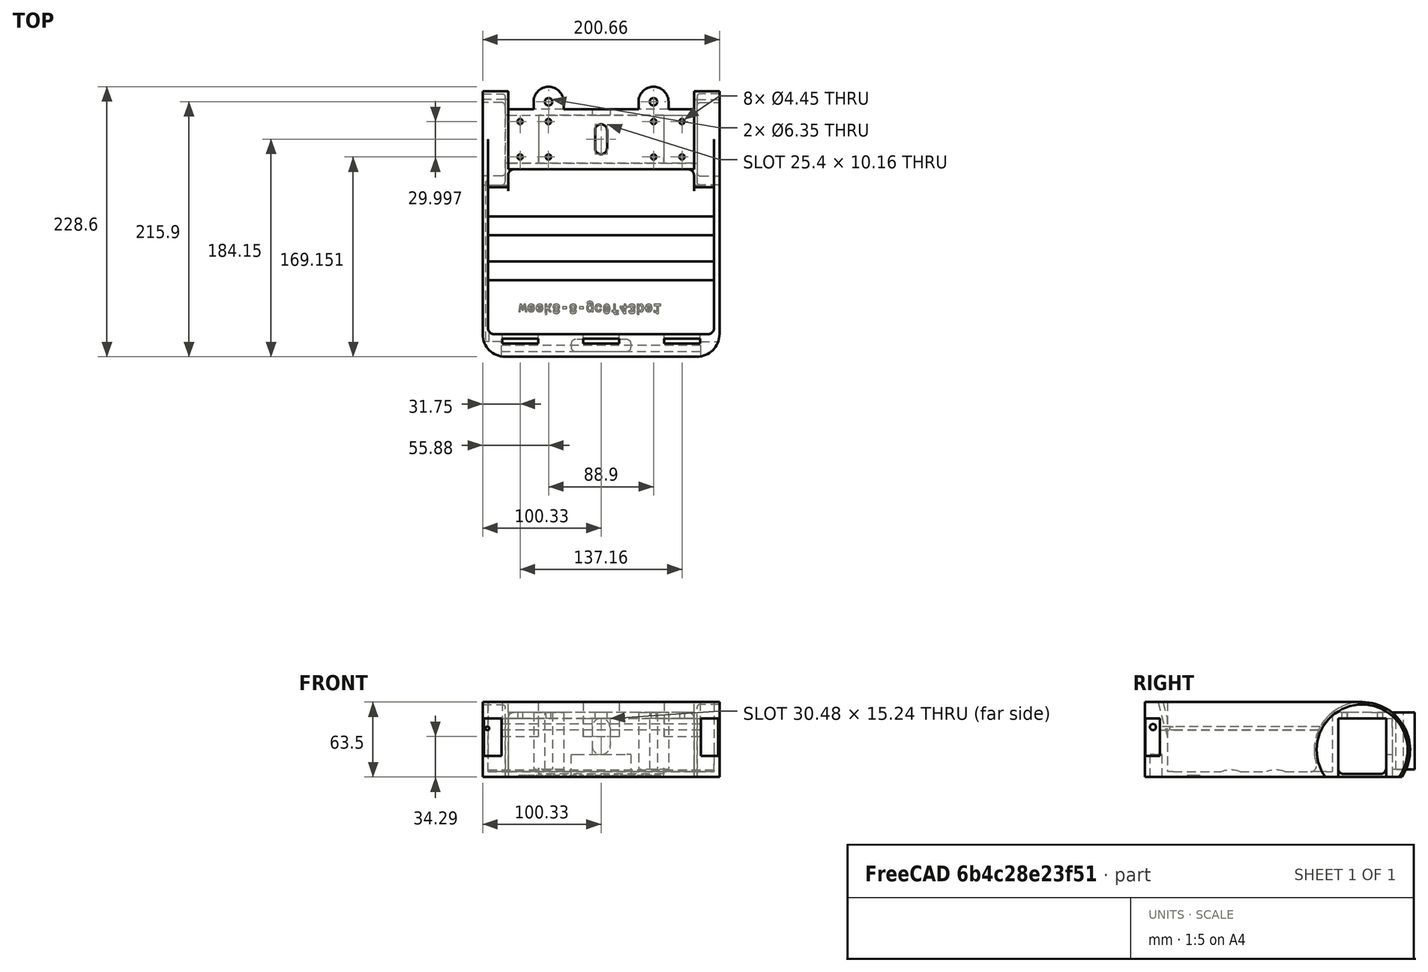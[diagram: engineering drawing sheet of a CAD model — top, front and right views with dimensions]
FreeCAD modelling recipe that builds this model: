
FCSTD DOCUMENT  (FreeCAD 0.20R27936 (Git))
Label: Frame
License: All rights reserved
LicenseURL: http://en.wikipedia.org/wiki/All_rights_reserved
objects: Sketcher::SketchObject×18, PartDesign::Pad×12, PartDesign::Pocket×7, PartDesign::Fillet×4, PartDesign::Plane×2, Part::Part2DObjectPython×1, PartDesign::Body×1
note: 68 computed .brp shape members not serialized (recipe doc carries the construction recipe); baked Part::Feature solids carry a one-line shape summary decoded from their .brp

FEATURE [Sketcher::SketchObject] Sketch
  FullyConstrained = true
  MapMode = 5
  Support = -> [XY_Plane]
  sketch-geometry (29):
    g0: LineSegment StartX=-78.74 StartY=-20.32 StartZ=0 EndX=-78.74 EndY=20.32 EndZ=0
    g1: LineSegment StartX=-78.74 StartY=20.32 StartZ=0 EndX=78.74 EndY=20.32 EndZ=0
    g2: LineSegment StartX=78.74 StartY=20.32 StartZ=0 EndX=78.74 EndY=-20.32 EndZ=0
    g3: LineSegment StartX=78.74 StartY=-20.32 StartZ=0 EndX=-78.74 EndY=-20.32 EndZ=0
    g4: GeomPoint X=0 Y=0 Z=0
    g5: LineSegment StartX=-68.58 StartY=14.9987 StartZ=0 EndX=-44.577 EndY=14.9987 EndZ=0
    g6: LineSegment StartX=-44.577 StartY=14.9987 StartZ=0 EndX=-44.577 EndY=-14.9987 EndZ=0
    g7: LineSegment StartX=-44.577 StartY=-14.9987 StartZ=0 EndX=-68.58 EndY=-14.9987 EndZ=0
    g8: LineSegment StartX=-68.58 StartY=-14.9987 StartZ=0 EndX=-68.58 EndY=14.9987 EndZ=0
    g9: LineSegment StartX=44.577 StartY=14.9987 StartZ=0 EndX=68.58 EndY=14.9987 EndZ=0
    g10: LineSegment StartX=68.58 StartY=14.9987 StartZ=0 EndX=68.58 EndY=-14.9987 EndZ=0
    g11: LineSegment StartX=68.58 StartY=-14.9987 StartZ=0 EndX=44.577 EndY=-14.9987 EndZ=0
    g12: LineSegment StartX=44.577 StartY=-14.9987 StartZ=0 EndX=44.577 EndY=14.9987 EndZ=0
    g13: Circle CenterX=-68.58 CenterY=14.9987 CenterZ=0 NormalX=0 NormalY=0 NormalZ=1 AngleXU=0 Radius=2.2225
    g14: Circle CenterX=-44.577 CenterY=14.9987 CenterZ=0 NormalX=0 NormalY=0 NormalZ=1 AngleXU=0 Radius=2.2225
    g15: Circle CenterX=-68.58 CenterY=-14.9987 CenterZ=0 NormalX=0 NormalY=0 NormalZ=1 AngleXU=0 Radius=2.2225
    g16: Circle CenterX=-44.577 CenterY=-14.9987 CenterZ=0 NormalX=0 NormalY=0 NormalZ=1 AngleXU=0 Radius=2.2225
    g17: Circle CenterX=44.577 CenterY=14.9987 CenterZ=0 NormalX=0 NormalY=0 NormalZ=1 AngleXU=0 Radius=2.2225
    g18: Circle CenterX=44.577 CenterY=-14.9987 CenterZ=0 NormalX=0 NormalY=0 NormalZ=1 AngleXU=0 Radius=2.2225
    g19: Circle CenterX=68.58 CenterY=14.9987 CenterZ=0 NormalX=0 NormalY=0 NormalZ=1 AngleXU=0 Radius=2.2225
    g20: Circle CenterX=68.58 CenterY=-14.9987 CenterZ=0 NormalX=0 NormalY=0 NormalZ=1 AngleXU=0 Radius=2.2225
    g21: LineSegment StartX=-68.58 StartY=0 StartZ=0 EndX=-78.74 EndY=0 EndZ=0
    g22: LineSegment StartX=68.58 StartY=0 StartZ=0 EndX=78.74 EndY=0 EndZ=0
    g23: ArcOfCircle CenterX=0 CenterY=7.62 CenterZ=0 NormalX=0 NormalY=0 NormalZ=1 AngleXU=0 Radius=5.08 StartAngle=0 EndAngle=3.14159
    g24: ArcOfCircle CenterX=0 CenterY=-7.62 CenterZ=0 NormalX=0 NormalY=0 NormalZ=1 AngleXU=0 Radius=5.08 StartAngle=3.14159 EndAngle=6.28319
    g25: LineSegment StartX=-5.08 StartY=7.62 StartZ=0 EndX=-5.08 EndY=-7.62 EndZ=0
    g26: LineSegment StartX=5.08 StartY=7.62 StartZ=0 EndX=5.08 EndY=-7.62 EndZ=0
    g27: LineSegment StartX=0 StartY=7.62 StartZ=0 EndX=0 EndY=0 EndZ=0
    g28: LineSegment StartX=0 StartY=0 StartZ=0 EndX=0 EndY=-7.62 EndZ=0
  constraints (70):
    c: Coincident(g0,g1)
    c: Coincident(g1,g2)
    c: Coincident(g2,g3)
    c: Coincident(g3,g0)
    c: Horizontal(g1)
    c: Horizontal(g3)
    c: Vertical(g0)
    c: Vertical(g2)
    c: Symmetric(g1,g0,g4)
    c: Coincident(g4,g-1)
    c: Distance(g1) = 157.48
    c: Distance(g0) = 40.64
    c: Coincident(g5,g6)
    c: Coincident(g6,g7)
    c: Coincident(g7,g8)
    c: Coincident(g8,g5)
    c: Horizontal(g5)
    c: Horizontal(g7)
    c: Vertical(g8)
    c: Coincident(g9,g10)
    c: Coincident(g10,g11)
    c: Coincident(g11,g12)
    c: Coincident(g12,g9)
    c: Horizontal(g9)
    c: Horizontal(g11)
    c: Vertical(g10)
    c: Distance(g6) = 29.9974
    c: Symmetric(g5,g6,g-1)
    c: Equal(g12,g6)
    c: Symmetric(g9,g11,g-1)
    c: Equal(g9,g5)
    c: Distance(g5) = 24.003
    c: Coincident(g13,g5)
    c: Coincident(g14,g5)
    c: Coincident(g15,g7)
    c: Coincident(g16,g6)
    c: Coincident(g17,g9)
    c: Coincident(g18,g11)
    c: Coincident(g19,g9)
    c: Coincident(g20,g10)
    c: Equal(g20,g18)
    c: Equal(g18,g17)
    c: Equal(g17,g19)
    c: Equal(g19,g14)
    c: Equal(g14,g13)
    c: Equal(g13,g15)
    c: Equal(g15,g16)
    c: Diameter(g16) = 4.445
    c: PointOnObject(g21,g8)
    c: PointOnObject(g21,g0)
    c: PointOnObject(g22,g10)
    c: PointOnObject(g22,g2)
    c: Tangent(g-1,g22)
    c: Tangent(g-1,g21)
    c: Equal(g21,g22)
    c: Distance(g21) = 10.16
    c: PointOnObject(g23,g-2)
    c: PointOnObject(g24,g-2)
    c: Vertical(g25)
    c: Tangent(g26,g24) = 1.5708
    c: Tangent(g26,g23) = 1.5708
    c: Tangent(g25,g23) = -1.5708
    c: Tangent(g25,g24) = -1.5708
    c: Radius(g23) = 5.08
    c: Coincident(g27,g23)
    c: Coincident(g27,g4)
    c: Coincident(g28,g4)
    c: Coincident(g28,g24)
    c: Equal(g28,g27)
    c: Distance(g27) = 7.62
FEATURE [PartDesign::Pad] Pad
  Direction = (0,0,1)
  Length = 5.08
  Length2 = 10.0076
  Profile = -> Sketch
  ReferenceAxis = -> Sketch [N_Axis]
  Type = 0
FEATURE [Sketcher::SketchObject] Sketch001
  ExternalGeometry = -> [Pad]
  FullyConstrained = true
  MapMode = 5
  Placement = pos=(0,0,5.08) rot=(0,0,1;0rad)
  Support = -> [Pad]
  sketch-geometry (8):
    g0: LineSegment StartX=-78.74 StartY=20.32 StartZ=0 EndX=78.74 EndY=20.32 EndZ=0
    g1: LineSegment StartX=78.74 StartY=20.32 StartZ=0 EndX=78.74 EndY=25.4 EndZ=0
    g2: LineSegment StartX=78.74 StartY=25.4 StartZ=0 EndX=-78.74 EndY=25.4 EndZ=0
    g3: LineSegment StartX=-78.74 StartY=25.4 StartZ=0 EndX=-78.74 EndY=20.32 EndZ=0
    g4: LineSegment StartX=-78.74 StartY=-20.32 StartZ=0 EndX=78.74 EndY=-20.32 EndZ=0
    g5: LineSegment StartX=78.74 StartY=-20.32 StartZ=0 EndX=78.74 EndY=-25.4 EndZ=0
    g6: LineSegment StartX=78.74 StartY=-25.4 StartZ=0 EndX=-78.74 EndY=-25.4 EndZ=0
    g7: LineSegment StartX=-78.74 StartY=-25.4 StartZ=0 EndX=-78.74 EndY=-20.32 EndZ=0
  constraints (20):
    c: Coincident(g0,g1)
    c: Coincident(g1,g2)
    c: Coincident(g2,g3)
    c: Coincident(g3,g0)
    c: Horizontal(g0)
    c: Horizontal(g2)
    c: Vertical(g3)
    c: Coincident(g0,g-4)
    c: Coincident(g4,g5)
    c: Coincident(g5,g6)
    c: Coincident(g6,g7)
    c: Coincident(g7,g4)
    c: Horizontal(g4)
    c: Horizontal(g6)
    c: Vertical(g7)
    c: Coincident(g4,g-5)
    c: Tangent(g5,g-3)
    c: Tangent(g-3,g1)
    c: Equal(g1,g5)
    c: Distance(g3) = 5.08
FEATURE [PartDesign::Pad] Pad001
  BaseFeature = -> Pad
  Direction = (0,0,1)
  Length = 54.61
  Length2 = 10.0076
  Profile = -> Sketch001
  ReferenceAxis = -> Sketch001 [N_Axis]
  Reversed = true
  Type = 0
FEATURE [Sketcher::SketchObject] Sketch002
  ExternalGeometry = -> [Pad001]
  FullyConstrained = true
  MapMode = 5
  Placement = pos=(0,20.32,0) rot=(1,0,0;1.5708rad)
  Support = -> [Pad001]
  sketch-geometry (4):
    g0: LineSegment StartX=-53.0225 StartY=-49.53 StartZ=0 EndX=53.0225 EndY=-49.53 EndZ=0
    g1: LineSegment StartX=53.0225 StartY=-49.53 StartZ=0 EndX=53.0225 EndY=-46.99 EndZ=0
    g2: LineSegment StartX=53.0225 StartY=-46.99 StartZ=0 EndX=-53.0225 EndY=-46.99 EndZ=0
    g3: LineSegment StartX=-53.0225 StartY=-46.99 StartZ=0 EndX=-53.0225 EndY=-49.53 EndZ=0
  constraints (11):
    c: Coincident(g0,g1)
    c: Coincident(g1,g2)
    c: Coincident(g2,g3)
    c: Coincident(g3,g0)
    c: Horizontal(g2)
    c: Vertical(g1)
    c: Vertical(g3)
    c: Distance(g0) = 106.045
    c: Tangent(g0,g-3)
    c: Symmetric(g0,g0,g-2)
    c: Distance(g3) = 2.54
FEATURE [PartDesign::Pad] Pad002
  BaseFeature = -> Pad001
  Direction = (0,-1,2e-16)
  Length = 10.0076
  Length2 = 10.0076
  Profile = -> Sketch002
  ReferenceAxis = -> Sketch002 [N_Axis]
  Type = 3
  UpToFace = -> Pad001 [Face7]
FEATURE [PartDesign::Fillet] Fillet
  Base = -> Pad002 [Edge49,Edge61]
  BaseFeature = -> Pad002
  Radius = 5.08
  SupportTransform = false
  UseAllEdges = false
FEATURE [Sketcher::SketchObject] Sketch003
  ExternalGeometry = -> [Fillet]
  FullyConstrained = true
  MapMode = 5
  Placement = pos=(-78.74,0,0) rot=(0.57735,-0.57735,-0.57735;2.0944rad)
  Support = -> [Fillet]
  sketch-geometry (7):
    g0: Circle CenterX=0 CenterY=-26.67 CenterZ=0 NormalX=0 NormalY=0 NormalZ=1 AngleXU=0 Radius=40.64
    g1: ArcOfCircle CenterX=0 CenterY=-26.67 CenterZ=0 NormalX=0 NormalY=0 NormalZ=1 AngleXU=0 Radius=40.64 StartAngle=5.68578 EndAngle=10.0222
    g2: LineSegment StartX=-33.601 StartY=-49.53 StartZ=0 EndX=-20.32 EndY=-49.53 EndZ=0
    g3: LineSegment StartX=-20.32 StartY=-49.53 StartZ=0 EndX=-20.32 EndY=0 EndZ=0
    g4: LineSegment StartX=-20.32 StartY=0 StartZ=0 EndX=20.32 EndY=0 EndZ=0
    g5: LineSegment StartX=20.32 StartY=0 StartZ=0 EndX=20.32 EndY=-49.53 EndZ=0
    g6: LineSegment StartX=20.32 StartY=-49.53 StartZ=0 EndX=33.601 EndY=-49.53 EndZ=0
  constraints (19):
    c: PointOnObject(g0,g-2)
    c: Distance(g0,g-3) = 31.75
    c: Diameter(g0) = 81.28
    c: Coincident(g1,g0)
    c: PointOnObject(g1,g0)
    c: Coincident(g2,g1)
    c: Coincident(g6,g1)
    c: Coincident(g3,g-4)
    c: PointOnObject(g3,g-1)
    c: Vertical(g3)
    c: Coincident(g4,g3)
    c: PointOnObject(g4,g-1)
    c: Coincident(g5,g4)
    c: Coincident(g5,g-4)
    c: Vertical(g5)
    c: Tangent(g6,g-4) = -1.5708
    c: Coincident(g6,g5)
    c: Coincident(g2,g3)
    c: Tangent(g2,g-4)
FEATURE [PartDesign::Pad] Pad003
  BaseFeature = -> Fillet
  Direction = (-1,0,0)
  Length = 2.54
  Length2 = 10.0076
  Profile = -> Sketch003
  ReferenceAxis = -> Sketch003 [N_Axis]
  Type = 0
FEATURE [Sketcher::SketchObject] Sketch004
  ExternalGeometry = -> [Pad003]
  FullyConstrained = true
  MapMode = 5
  Placement = pos=(78.74,0,0) rot=(0.57735,0.57735,0.57735;2.0944rad)
  Support = -> [Pad003]
  sketch-geometry (6):
    g0: LineSegment StartX=-20.32 StartY=-49.53 StartZ=0 EndX=-33.601 EndY=-49.53 EndZ=0
    g1: LineSegment StartX=20.32 StartY=-49.53 StartZ=0 EndX=33.601 EndY=-49.53 EndZ=0
    g2: LineSegment StartX=20.32 StartY=-49.53 StartZ=0 EndX=20.32 EndY=0 EndZ=0
    g3: LineSegment StartX=20.32 StartY=0 StartZ=0 EndX=-20.32 EndY=0 EndZ=0
    g4: LineSegment StartX=-20.32 StartY=0 StartZ=0 EndX=-20.32 EndY=-49.53 EndZ=0
    g5: ArcOfCircle CenterX=0 CenterY=-26.67 CenterZ=0 NormalX=0 NormalY=0 NormalZ=1 AngleXU=0 Radius=40.64 StartAngle=5.68578 EndAngle=10.0222
  constraints (16):
    c: Coincident(g0,g-3)
    c: Coincident(g0,g-5)
    c: Coincident(g1,g-4)
    c: Horizontal(g1)
    c: Coincident(g2,g1)
    c: PointOnObject(g2,g-1)
    c: Vertical(g2)
    c: Coincident(g3,g2)
    c: PointOnObject(g3,g-1)
    c: Coincident(g4,g3)
    c: Coincident(g4,g0)
    c: Vertical(g4)
    c: PointOnObject(g5,g-2)
    c: Coincident(g5,g0)
    c: Coincident(g5,g1)
    c: Equal(g5,g-5)
FEATURE [PartDesign::Pad] Pad004
  BaseFeature = -> Pad003
  Direction = (1,0,0)
  Length = 2.54
  Length2 = 10.0076
  Profile = -> Sketch004
  ReferenceAxis = -> Sketch004 [N_Axis]
  Type = 0
FEATURE [Sketcher::SketchObject] Sketch005
  ExternalGeometry = -> [Pad004]
  FullyConstrained = true
  MapMode = 5
  Placement = pos=(-81.28,0,0) rot=(0.57735,-0.57735,-0.57735;2.0944rad)
  Support = -> [Pad004]
  sketch-geometry (4):
    g0: ArcOfCircle CenterX=4.7e-15 CenterY=-26.67 CenterZ=0 NormalX=0 NormalY=0 NormalZ=1 AngleXU=0 Radius=40.64 StartAngle=5.68578 EndAngle=10.0222
    g1: ArcOfCircle CenterX=4.7e-15 CenterY=-26.67 CenterZ=0 NormalX=0 NormalY=0 NormalZ=1 AngleXU=0 Radius=38.5664 StartAngle=5.64872 EndAngle=10.0592
    g2: LineSegment StartX=-33.601 StartY=-49.53 StartZ=0 EndX=-31.061 EndY=-49.53 EndZ=0
    g3: LineSegment StartX=31.061 StartY=-49.53 StartZ=0 EndX=33.601 EndY=-49.53 EndZ=0
  constraints (11):
    c: Coincident(g1,g0)
    c: Coincident(g2,g0)
    c: Coincident(g2,g1)
    c: Coincident(g3,g1)
    c: Coincident(g3,g0)
    c: Horizontal(g3)
    c: Horizontal(g2)
    c: Distance(g2) = 2.54
    c: Coincident(g0,g-3)
    c: Coincident(g0,g-3)
    c: Equal(g0,g-3)
FEATURE [PartDesign::Pad] Pad005
  BaseFeature = -> Pad004
  Direction = (-1,0,0)
  Length = 19.05
  Length2 = 10.0076
  Profile = -> Sketch005
  ReferenceAxis = -> Sketch005 [N_Axis]
  Type = 0
FEATURE [Sketcher::SketchObject] Sketch006
  ExternalGeometry = -> [Pad005]
  FullyConstrained = true
  MapMode = 5
  Placement = pos=(81.28,0,0) rot=(0.57735,0.57735,0.57735;2.0944rad)
  Support = -> [Pad005]
  sketch-geometry (4):
    g0: ArcOfCircle CenterX=-3.6e-15 CenterY=-26.67 CenterZ=0 NormalX=0 NormalY=0 NormalZ=1 AngleXU=0 Radius=40.64 StartAngle=5.68578 EndAngle=10.0222
    g1: ArcOfCircle CenterX=-3.6e-15 CenterY=-26.67 CenterZ=0 NormalX=0 NormalY=0 NormalZ=1 AngleXU=0 Radius=38.5664 StartAngle=5.64872 EndAngle=10.0592
    g2: LineSegment StartX=31.061 StartY=-49.53 StartZ=0 EndX=33.601 EndY=-49.53 EndZ=0
    g3: LineSegment StartX=-33.601 StartY=-49.53 StartZ=0 EndX=-31.061 EndY=-49.53 EndZ=0
  constraints (10):
    c: Coincident(g0,g-4)
    c: Coincident(g0,g-4)
    c: Coincident(g0,g-4)
    c: Coincident(g1,g0)
    c: Coincident(g1,g-3)
    c: Coincident(g1,g-3)
    c: Coincident(g2,g1)
    c: Coincident(g2,g0)
    c: Coincident(g3,g0)
    c: Coincident(g3,g1)
FEATURE [PartDesign::Pad] Pad006
  BaseFeature = -> Pad005
  Direction = (1,0,0)
  Length = 19.05
  Length2 = 10.0076
  Profile = -> Sketch006
  ReferenceAxis = -> Sketch006 [N_Axis]
  Type = 0
FEATURE [PartDesign::Fillet] Fillet001
  Base = -> Pad006 [Edge101,Edge71]
  BaseFeature = -> Pad006
  Radius = 2.54
  SupportTransform = false
  UseAllEdges = false
FEATURE [PartDesign::Plane] DatumPlane
  AttachmentOffset = pos=(0,0,165.1) rot=(0,0,1;0rad)
  Length = 60
  MapMode = 5
  Placement = pos=(0,-165.1,-3.67e-14) rot=(1,0,0;1.5708rad)
  ResizeMode = 0
  Support = -> [XZ_Plane]
  Width = 60
FEATURE [Sketcher::SketchObject] Sketch007
  ExternalGeometry = -> [Fillet001]
  FullyConstrained = true
  MapMode = 5
  Placement = pos=(0,-165.1,-3.67e-14) rot=(1,0,0;1.5708rad)
  Support = -> [DatumPlane]
  sketch-geometry (9):
    g0: LineSegment StartX=-100.33 StartY=13.97 StartZ=0 EndX=-100.33 EndY=-49.53 EndZ=0
    g1: LineSegment StartX=-100.33 StartY=-49.53 StartZ=0 EndX=100.33 EndY=-49.53 EndZ=0
    g2: LineSegment StartX=100.33 StartY=-49.53 StartZ=0 EndX=100.33 EndY=13.97 EndZ=0
    g3: LineSegment StartX=100.33 StartY=13.97 StartZ=0 EndX=95.758 EndY=13.97 EndZ=0
    g4: LineSegment StartX=95.758 StartY=13.97 StartZ=0 EndX=95.758 EndY=-44.958 EndZ=0
    g5: LineSegment StartX=95.758 StartY=-44.958 StartZ=0 EndX=-95.758 EndY=-44.958 EndZ=0
    g6: LineSegment StartX=-95.758 StartY=-44.958 StartZ=0 EndX=-95.758 EndY=13.97 EndZ=0
    g7: LineSegment StartX=-95.758 StartY=13.97 StartZ=0 EndX=-100.33 EndY=13.97 EndZ=0
    g8: LineSegment StartX=0 StartY=-49.53 StartZ=0 EndX=0 EndY=-44.958 EndZ=0
  constraints (23):
    c: Coincident(g0,g-3)
    c: Coincident(g0,g-3)
    c: Coincident(g1,g0)
    c: Coincident(g1,g-4)
    c: Coincident(g2,g1)
    c: Vertical(g2)
    c: Coincident(g3,g2)
    c: Horizontal(g3)
    c: Coincident(g4,g3)
    c: Vertical(g4)
    c: Coincident(g5,g4)
    c: Horizontal(g5)
    c: Coincident(g6,g5)
    c: Vertical(g6)
    c: Coincident(g7,g6)
    c: Coincident(g7,g0)
    c: PointOnObject(g8,g1)
    c: PointOnObject(g8,g5)
    c: Tangent(g8,g-2) = -1.5708
    c: Equal(g8,g7)
    c: Equal(g7,g3)
    c: Distance(g7) = 4.572
    c: Tangent(g3,g7)
FEATURE [PartDesign::Pad] Pad007
  BaseFeature = -> Fillet001
  Direction = (0,-1,-2e-16)
  Length = 10.0076
  Length2 = 10.0076
  Profile = -> Sketch007
  ReferenceAxis = -> Sketch007 [N_Axis]
  Reversed = true
  Type = 3
  UpToFace = -> Fillet001 [Face61]
FEATURE [Sketcher::SketchObject] Sketch008
  ExternalGeometry = -> [Pad007]
  FullyConstrained = true
  MapMode = 5
  Placement = pos=(0,-25.4,0) rot=(1,0,0;1.5708rad)
  Support = -> [Pad007]
  sketch-geometry (4):
    g0: LineSegment StartX=78.74 StartY=-44.958 StartZ=0 EndX=-78.74 EndY=-44.958 EndZ=0
    g1: LineSegment StartX=-78.74 StartY=-44.958 StartZ=0 EndX=-78.74 EndY=-49.53 EndZ=0
    g2: LineSegment StartX=-78.74 StartY=-49.53 StartZ=0 EndX=78.74 EndY=-49.53 EndZ=0
    g3: LineSegment StartX=78.74 StartY=-49.53 StartZ=0 EndX=78.74 EndY=-44.958 EndZ=0
  constraints (10):
    c: Coincident(g0,g1)
    c: Coincident(g1,g2)
    c: Coincident(g2,g3)
    c: Coincident(g3,g0)
    c: Horizontal(g0)
    c: Horizontal(g2)
    c: Vertical(g1)
    c: Vertical(g3)
    c: Coincident(g0,g-4)
    c: Coincident(g1,g-3)
FEATURE [PartDesign::Pad] Pad008
  BaseFeature = -> Pad007
  Direction = (0,-1,2e-16)
  Length = 12.7
  Length2 = 10.0076
  Profile = -> Sketch008
  ReferenceAxis = -> Sketch008 [N_Axis]
  Type = 0
FEATURE [Sketcher::SketchObject] Sketch009
  ExternalGeometry = -> [Pad008]
  FullyConstrained = false
  MapMode = 5
  Placement = pos=(95.758,0,0) rot=(0.57735,-0.57735,-0.57735;2.0944rad)
  Support = -> [Pad008]
  sketch-geometry (5):
    g0: ArcOfCircle CenterX=73.2715 CenterY=-66.3764 CenterZ=0 NormalX=0 NormalY=0 NormalZ=1 AngleXU=0 Radius=22.86 StartAngle=1.21376 EndAngle=1.92783
    g1: ArcOfCircle CenterX=111.371 CenterY=-66.3764 CenterZ=0 NormalX=0 NormalY=0 NormalZ=1 AngleXU=0 Radius=22.86 StartAngle=1.21376 EndAngle=1.92783
    g2: LineSegment StartX=73.2715 StartY=-66.3764 StartZ=0 EndX=111.371 EndY=-66.3764 EndZ=0
    g3: LineSegment StartX=65.2819 StartY=-44.958 StartZ=0 EndX=81.2611 EndY=-44.958 EndZ=0
    g4: LineSegment StartX=103.382 StartY=-44.958 StartZ=0 EndX=119.361 EndY=-44.958 EndZ=0
  constraints (14):
    c: PointOnObject(g0,g-3)
    c: PointOnObject(g0,g-3)
    c: PointOnObject(g1,g-3)
    c: PointOnObject(g1,g-3)
    c: Equal(g1,g0)
    c: Coincident(g2,g0)
    c: Coincident(g2,g1)
    c: Horizontal(g2)
    c: Distance(g2) = 38.1
    c: Radius(g0) = 22.86
    c: Coincident(g3,g0)
    c: Coincident(g3,g0)
    c: Coincident(g4,g1)
    c: Coincident(g4,g1)
FEATURE [PartDesign::Pad] Pad009
  BaseFeature = -> Pad008
  Direction = (-1,0,0)
  Length = 10.0076
  Length2 = 10.0076
  Profile = -> Sketch009
  ReferenceAxis = -> Sketch009 [N_Axis]
  Type = 3
  UpToFace = -> Pad008 [Face37]
FEATURE [Sketcher::SketchObject] Sketch010
  ExternalGeometry = -> [Pad009]
  FullyConstrained = true
  MapMode = 5
  Placement = pos=(1.05e-14,1.1e-14,-49.53) rot=(1,0,0;3.14159rad)
  Support = -> [Pad009]
  sketch-geometry (4):
    g0: ArcOfCircle CenterX=-81.28 CenterY=165.1 CenterZ=0 NormalX=0 NormalY=0 NormalZ=1 AngleXU=0 Radius=19.05 StartAngle=1.5708 EndAngle=3.14159
    g1: ArcOfCircle CenterX=81.28 CenterY=165.1 CenterZ=0 NormalX=0 NormalY=0 NormalZ=1 AngleXU=0 Radius=19.05 StartAngle=-9e-16 EndAngle=1.5708
    g2: LineSegment StartX=100.33 StartY=165.1 StartZ=0 EndX=-100.33 EndY=165.1 EndZ=0
    g3: LineSegment StartX=-81.28 StartY=184.15 StartZ=0 EndX=81.28 EndY=184.15 EndZ=0
  constraints (10):
    c: Coincident(g2,g1)
    c: Coincident(g2,g0)
    c: Horizontal(g3)
    c: Tangent(g3,g1) = 1.5708
    c: Tangent(g3,g0) = 1.5708
    c: Coincident(g0,g-4)
    c: Coincident(g1,g-3)
    c: Radius(g1) = 19.05
    c: PointOnObject(g1,g2)
    c: Equal(g0,g1)
FEATURE [PartDesign::Pad] Pad010
  BaseFeature = -> Pad009
  Direction = (2e-16,2e-16,-1)
  Length = 10.0076
  Length2 = 10.0076
  Profile = -> Sketch010
  ReferenceAxis = -> Sketch010 [N_Axis]
  Type = 3
  UpToFace = -> Pad009 [Face38]
FEATURE [PartDesign::Plane] DatumPlane001
  AttachmentOffset = pos=(0,0,50.8) rot=(1,0,0;0.261799rad)
  Length = 61.0668
  MapMode = 5
  Placement = pos=(1.258e-13,-1.44e-14,64.77) rot=(1,0,0;0.261799rad)
  ResizeMode = 0
  Support = -> [Pad010]
  Width = 72.3041
FEATURE [Sketcher::SketchObject] Sketch011
  ExternalGeometry = -> [Pad010]
  FullyConstrained = true
  MapMode = 5
  Placement = pos=(1.258e-13,-1.78e-14,64.77) rot=(1,0,0;0.261799rad)
  Support = -> [DatumPlane001]
  sketch-geometry (14):
    g0: LineSegment StartX=-83.82 StartY=-176.178 StartZ=0 EndX=-53.34 EndY=-176.178 EndZ=0
    g1: LineSegment StartX=-53.34 StartY=-176.178 StartZ=0 EndX=-53.34 EndY=-180.242 EndZ=0
    g2: LineSegment StartX=-53.34 StartY=-180.242 StartZ=0 EndX=-83.82 EndY=-180.242 EndZ=0
    g3: LineSegment StartX=-83.82 StartY=-180.242 StartZ=0 EndX=-83.82 EndY=-176.178 EndZ=0
    g4: LineSegment StartX=-15.24 StartY=-176.178 StartZ=0 EndX=15.24 EndY=-176.178 EndZ=0
    g5: LineSegment StartX=15.24 StartY=-176.178 StartZ=0 EndX=15.24 EndY=-180.242 EndZ=0
    g6: LineSegment StartX=15.24 StartY=-180.242 StartZ=0 EndX=-15.24 EndY=-180.242 EndZ=0
    g7: LineSegment StartX=-15.24 StartY=-180.242 StartZ=0 EndX=-15.24 EndY=-176.178 EndZ=0
    g8: LineSegment StartX=53.34 StartY=-176.178 StartZ=0 EndX=83.82 EndY=-176.178 EndZ=0
    g9: LineSegment StartX=83.82 StartY=-176.178 StartZ=0 EndX=83.82 EndY=-180.242 EndZ=0
    g10: LineSegment StartX=83.82 StartY=-180.242 StartZ=0 EndX=53.34 EndY=-180.242 EndZ=0
    g11: LineSegment StartX=53.34 StartY=-180.242 StartZ=0 EndX=53.34 EndY=-176.178 EndZ=0
    g12: LineSegment StartX=53.34 StartY=-176.178 StartZ=0 EndX=15.24 EndY=-176.178 EndZ=0
    g13: LineSegment StartX=-15.24 StartY=-176.178 StartZ=0 EndX=-53.34 EndY=-176.178 EndZ=0
  constraints (37):
    c: Coincident(g0,g1)
    c: Coincident(g1,g2)
    c: Coincident(g2,g3)
    c: Coincident(g3,g0)
    c: Horizontal(g2)
    c: Vertical(g1)
    c: Vertical(g3)
    c: Coincident(g4,g5)
    c: Coincident(g5,g6)
    c: Coincident(g6,g7)
    c: Coincident(g7,g4)
    c: Horizontal(g6)
    c: Vertical(g5)
    c: Vertical(g7)
    c: Coincident(g8,g9)
    c: Coincident(g9,g10)
    c: Coincident(g10,g11)
    c: Coincident(g11,g8)
    c: Horizontal(g10)
    c: Vertical(g9)
    c: Vertical(g11)
    c: Equal(g11,g5)
    c: Equal(g5,g1)
    c: Tangent(g0,g4)
    c: Tangent(g4,g8)
    c: Distance(g9) = 4.064
    c: Equal(g8,g4)
    c: Equal(g4,g0)
    c: Symmetric(g4,g4,g-2)
    c: Coincident(g12,g8)
    c: Coincident(g12,g4)
    c: Coincident(g13,g4)
    c: Coincident(g13,g0)
    c: Equal(g13,g12)
    c: Distance(g4,g-3) = 3.556
    c: Distance(g13) = 38.1
    c: Distance(g6) = 30.48
FEATURE [PartDesign::Pocket] Pocket
  BaseFeature = -> Pad010
  Direction = (-1.9e-15,0.258819,-0.965926)
  Length = 55.8038
  Length2 = 5.0038
  Profile = -> Sketch011
  ReferenceAxis = -> Sketch011 [N_Axis]
  Type = 0
FEATURE [Sketcher::SketchObject] Sketch012
  FullyConstrained = true
  MapMode = 5
  Placement = pos=(0,-184.15,-4.09e-14) rot=(1,0,0;1.5708rad)
  Support = -> [Pocket]
  sketch-geometry (8):
    g0: LineSegment StartX=84.455 StartY=0 StartZ=0 EndX=100.965 EndY=0 EndZ=0
    g1: LineSegment StartX=100.965 StartY=0 StartZ=0 EndX=100.965 EndY=-31.75 EndZ=0
    g2: LineSegment StartX=100.965 StartY=-31.75 StartZ=0 EndX=84.455 EndY=-31.75 EndZ=0
    g3: LineSegment StartX=84.455 StartY=-31.75 StartZ=0 EndX=84.455 EndY=0 EndZ=0
    g4: LineSegment StartX=-84.455 StartY=0 StartZ=0 EndX=-100.965 EndY=0 EndZ=0
    g5: LineSegment StartX=-100.965 StartY=0 StartZ=0 EndX=-100.965 EndY=-31.75 EndZ=0
    g6: LineSegment StartX=-100.965 StartY=-31.75 StartZ=0 EndX=-84.455 EndY=-31.75 EndZ=0
    g7: LineSegment StartX=-84.455 StartY=-31.75 StartZ=0 EndX=-84.455 EndY=0 EndZ=0
  constraints (22):
    c: Coincident(g0,g1)
    c: Coincident(g1,g2)
    c: Coincident(g2,g3)
    c: Coincident(g3,g0)
    c: Horizontal(g2)
    c: Vertical(g1)
    c: Vertical(g3)
    c: Coincident(g4,g5)
    c: Coincident(g5,g6)
    c: Coincident(g6,g7)
    c: Coincident(g7,g4)
    c: Horizontal(g6)
    c: Vertical(g5)
    c: Vertical(g7)
    c: Equal(g7,g3)
    c: Tangent(g0,g4)
    c: PointOnObject(g0,g-1)
    c: Distance(g3) = 31.75
    c: Distance(g2) = 16.51
    c: Symmetric(g4,g0,g-2)
    c: Distance(g4,g0) = 168.91
    c: Equal(g4,g0)
FEATURE [PartDesign::Pocket] Pocket001
  BaseFeature = -> Pocket
  Direction = (0,1,2e-16)
  Length = 12.7
  Length2 = 5.0038
  Profile = -> Sketch012
  ReferenceAxis = -> Sketch012 [N_Axis]
  Type = 0
FEATURE [Sketcher::SketchObject] Sketch013
  ExternalGeometry = -> [Pocket001]
  FullyConstrained = true
  MapMode = 5
  Placement = pos=(0,0,5.08) rot=(0,0,1;0rad)
  Support = -> [Pocket001]
  sketch-geometry (10):
    g0: ArcOfCircle CenterX=-44.45 CenterY=31.75 CenterZ=0 NormalX=0 NormalY=0 NormalZ=1 AngleXU=0 Radius=12.7 StartAngle=2e-16 EndAngle=3.14159
    g1: ArcOfCircle CenterX=44.45 CenterY=31.75 CenterZ=0 NormalX=0 NormalY=0 NormalZ=1 AngleXU=0 Radius=12.7 StartAngle=0 EndAngle=3.14159
    g2: Circle CenterX=-44.45 CenterY=31.75 CenterZ=0 NormalX=0 NormalY=0 NormalZ=1 AngleXU=0 Radius=3.175
    g3: Circle CenterX=44.45 CenterY=31.75 CenterZ=0 NormalX=0 NormalY=0 NormalZ=1 AngleXU=0 Radius=3.175
    g4: LineSegment StartX=-57.15 StartY=31.75 StartZ=0 EndX=-57.15 EndY=25.4 EndZ=0
    g5: LineSegment StartX=-57.15 StartY=25.4 StartZ=0 EndX=-31.75 EndY=25.4 EndZ=0
    g6: LineSegment StartX=-31.75 StartY=25.4 StartZ=0 EndX=-31.75 EndY=31.75 EndZ=0
    g7: LineSegment StartX=31.75 StartY=31.75 StartZ=0 EndX=31.75 EndY=25.4 EndZ=0
    g8: LineSegment StartX=31.75 StartY=25.4 StartZ=0 EndX=57.15 EndY=25.4 EndZ=0
    g9: LineSegment StartX=57.15 StartY=25.4 StartZ=0 EndX=57.15 EndY=31.75 EndZ=0
  constraints (24):
    c: Coincident(g2,g0)
    c: Coincident(g3,g1)
    c: Equal(g3,g2)
    c: Diameter(g2) = 6.35
    c: Radius(g0) = 12.7
    c: Equal(g0,g1)
    c: Vertical(g4)
    c: Coincident(g5,g4)
    c: Coincident(g6,g5)
    c: Vertical(g6)
    c: Coincident(g8,g7)
    c: Coincident(g9,g8)
    c: Vertical(g7)
    c: Vertical(g9)
    c: Tangent(g5,g-3)
    c: Tangent(g-3,g8)
    c: Symmetric(g5,g7,g-2)
    c: Tangent(g6,g0) = -1.5708
    c: Tangent(g4,g0) = -1.5708
    c: Tangent(g7,g1) = -1.5708
    c: Tangent(g9,g1) = -1.5708
    c: Distance(g9) = 6.35
    c: Equal(g6,g9)
    c: Distance(g0,g1) = 88.9
FEATURE [PartDesign::Pad] Pad011
  BaseFeature = -> Pocket001
  Direction = (0,0,1)
  Length = 10.0076
  Length2 = 10.0076
  Offset = 6.35
  Profile = -> Sketch013
  ReferenceAxis = -> Sketch013 [N_Axis]
  Type = 3
  UpToFace = -> Pocket001 [Face23]
FEATURE [PartDesign::Fillet] Fillet002
  Base = -> Pad011 [Edge242,Edge210,Edge175,Edge279]
  BaseFeature = -> Pad011
  Radius = 5.08
  SupportTransform = false
  UseAllEdges = false
FEATURE [PartDesign::Fillet] Fillet003
  Base = -> Fillet002 [Edge17,Edge22]
  BaseFeature = -> Fillet002
  Radius = 5.08
  SupportTransform = false
  UseAllEdges = false
FEATURE [Sketcher::SketchObject] Sketch014
  FullyConstrained = false
  MapMode = 5
  Placement = pos=(-84.455,0,0) rot=(0.57735,-0.57735,-0.57735;2.0944rad)
  Support = -> [Fillet003]
  sketch-geometry (1):
    g0: Circle CenterX=177.236 CenterY=-7.17251 CenterZ=0 NormalX=0 NormalY=0 NormalZ=1 AngleXU=0 Radius=2.54
  constraints (1):
    c: Diameter(g0) = 5.08
FEATURE [PartDesign::Pocket] Pocket002
  BaseFeature = -> Fillet003
  Direction = (1,0,0)
  Length = 5.0038
  Length2 = 5.0038
  Profile = -> Sketch014
  ReferenceAxis = -> Sketch014 [N_Axis]
  Type = 1
FEATURE [Sketcher::SketchObject] Sketch015
  ExternalGeometry = -> [Pocket002]
  FullyConstrained = false
  MapMode = 5
  Placement = pos=(0,-171.45,0) rot=(1,0,0;1.5708rad)
  Support = -> [Pocket002]
  sketch-geometry (1):
    g0: Circle CenterX=-96.266 CenterY=-8.29938 CenterZ=0 NormalX=0 NormalY=0 NormalZ=1 AngleXU=0 Radius=1.5875
  constraints (2):
    c: Diameter(g0) = 3.175
    c: Distance(g0,g-4) = 0.508
FEATURE [PartDesign::Pocket] Pocket003
  BaseFeature = -> Pocket002
  Direction = (0,1,-2e-16)
  Length = 0
  Length2 = 5.0038
  Profile = -> Sketch015
  ReferenceAxis = -> Sketch015 [N_Axis]
  Reversed = true
  Type = 3
  UpToFace = -> Pocket002 [Face35]
FEATURE [Part::Part2DObjectPython] ShapeString  # Draft 2D object (typed FeaturePython)
  FontFile = <path>
  MakeFace = true
  Placement = pos=(-69.85,-139.7,-49.53) rot=(1,0,0;3.14159rad)
  Size = 8.89
  String = week8-8-gc0f43be1
  Tracking = 0
FEATURE [PartDesign::Pocket] Pocket004  label="RevisionNumber"
  BaseFeature = -> Pocket003
  Direction = (0,0,1)
  Length = 1.27
  Length2 = 5.0038
  Profile = -> ShapeString
  ReferenceAxis = -> ShapeString [N_Axis]
  Type = 0
FEATURE [Sketcher::SketchObject] Sketch016
  FullyConstrained = true
  MapMode = 5
  Placement = pos=(1.05e-14,9.4e-15,-49.53) rot=(1,0,0;3.14159rad)
  Support = -> [Pocket004]
  sketch-geometry (8):
    g0: LineSegment StartX=-21.59 StartY=179.705 StartZ=0 EndX=21.59 EndY=179.705 EndZ=0
    g1: LineSegment StartX=25.4 StartY=175.895 StartZ=0 EndX=25.4 EndY=173.355 EndZ=0
    g2: LineSegment StartX=21.59 StartY=169.545 StartZ=0 EndX=-21.59 EndY=169.545 EndZ=0
    g3: LineSegment StartX=-25.4 StartY=173.355 StartZ=0 EndX=-25.4 EndY=175.895 EndZ=0
    g4: ArcOfCircle CenterX=21.59 CenterY=175.895 CenterZ=0 NormalX=0 NormalY=0 NormalZ=1 AngleXU=0 Radius=3.81 StartAngle=3e-16 EndAngle=1.5708
    g5: ArcOfCircle CenterX=21.59 CenterY=173.355 CenterZ=0 NormalX=0 NormalY=0 NormalZ=1 AngleXU=0 Radius=3.81 StartAngle=4.71239 EndAngle=6.28319
    g6: ArcOfCircle CenterX=-21.59 CenterY=175.895 CenterZ=0 NormalX=0 NormalY=0 NormalZ=1 AngleXU=0 Radius=3.81 StartAngle=1.5708 EndAngle=3.14159
    g7: ArcOfCircle CenterX=-21.59 CenterY=173.355 CenterZ=0 NormalX=0 NormalY=0 NormalZ=1 AngleXU=0 Radius=3.81 StartAngle=3.14159 EndAngle=4.71239
  constraints (19):
    c: Horizontal(g0)
    c: Horizontal(g2)
    c: Vertical(g1)
    c: Vertical(g3)
    c: Tangent(g0,g4) = 1.5708
    c: Tangent(g1,g4) = 1.5708
    c: Tangent(g1,g5) = 1.5708
    c: Tangent(g2,g5) = 1.5708
    c: Tangent(g3,g6) = 1.5708
    c: Tangent(g0,g6) = 1.5708
    c: Tangent(g3,g7) = 1.5708
    c: Tangent(g2,g7) = 1.5708
    c: Equal(g6,g7)
    c: Equal(g7,g5)
    c: Radius(g4) = 3.81
    c: Distance(g0,g2) = 10.16
    c: Symmetric(g6,g4,g-2)
    c: Distance(g1,g3) = 50.8
    c: Distance(g-1,g2) = 169.545
FEATURE [PartDesign::Pocket] Pocket005
  BaseFeature = -> Pocket004
  Direction = (-2e-16,-2e-16,1)
  Length = 19.05
  Length2 = 5.0038
  Profile = -> Sketch016
  ReferenceAxis = -> Sketch016 [N_Axis]
  Type = 0
FEATURE [Sketcher::SketchObject] Sketch017
  FullyConstrained = true
  MapMode = 5
  Placement = pos=(0,25.4,0) rot=(0,0.707107,0.707107;3.14159rad)
  Support = -> [Pocket005]
  sketch-geometry (4):
    g0: ArcOfCircle CenterX=0 CenterY=-7.62 CenterZ=0 NormalX=0 NormalY=0 NormalZ=1 AngleXU=0 Radius=7.62 StartAngle=6.28318 EndAngle=9.42478
    g1: ArcOfCircle CenterX=0 CenterY=-22.86 CenterZ=0 NormalX=0 NormalY=0 NormalZ=1 AngleXU=0 Radius=7.62 StartAngle=3.14159 EndAngle=6.28319
    g2: LineSegment StartX=-7.62 StartY=-7.62 StartZ=0 EndX=-7.62 EndY=-22.86 EndZ=0
    g3: LineSegment StartX=7.62 StartY=-7.62002 StartZ=0 EndX=7.62 EndY=-22.86 EndZ=0
  constraints (11):
    c: PointOnObject(g0,g-2)
    c: PointOnObject(g1,g-2)
    c: Coincident(g3,g0)
    c: Vertical(g3)
    c: Vertical(g2)
    c: Tangent(g2,g0) = -1.5708
    c: Tangent(g2,g1) = -1.5708
    c: Tangent(g3,g1) = 1.5708
    c: Distance(g3) = 15.24
    c: Radius(g0) = 7.62
    c: PointOnObject(g-1,g0)
FEATURE [PartDesign::Pocket] Pocket006
  BaseFeature = -> Pocket005
  Direction = (0,-1,2e-16)
  Length = 5.08
  Length2 = 5.0038
  Profile = -> Sketch017
  ReferenceAxis = -> Sketch017 [N_Axis]
  Type = 0
FEATURE [PartDesign::Body] Body  label="Frame Body"
  Group = -> [Sketch,Pad,Sketch001,Pad001,Sketch002,Pad002,Fillet,Sketch003,Pad003,Sketch004,Pad004,Sketch005,Pad005,Sketch006,Pad006,Fillet001,DatumPlane,Sketch007,Pad007,Sketch008,Pad008,Sketch009,Pad009,Sketch010,Pad010,DatumPlane001,Sketch011,Pocket,Sketch012,Pocket001,Sketch013,Pad011,Fillet002,Fillet003,Sketch014,Pocket002,Sketch015,Pocket003,ShapeString,Pocket004,Sketch016,Pocket005,Sketch017,Pocket006]
  Origin = -> Origin
  Tip = -> Pocket006
note: 1 file-system path scrubbed to <path> (originals preserved in the JSON sidecar)
